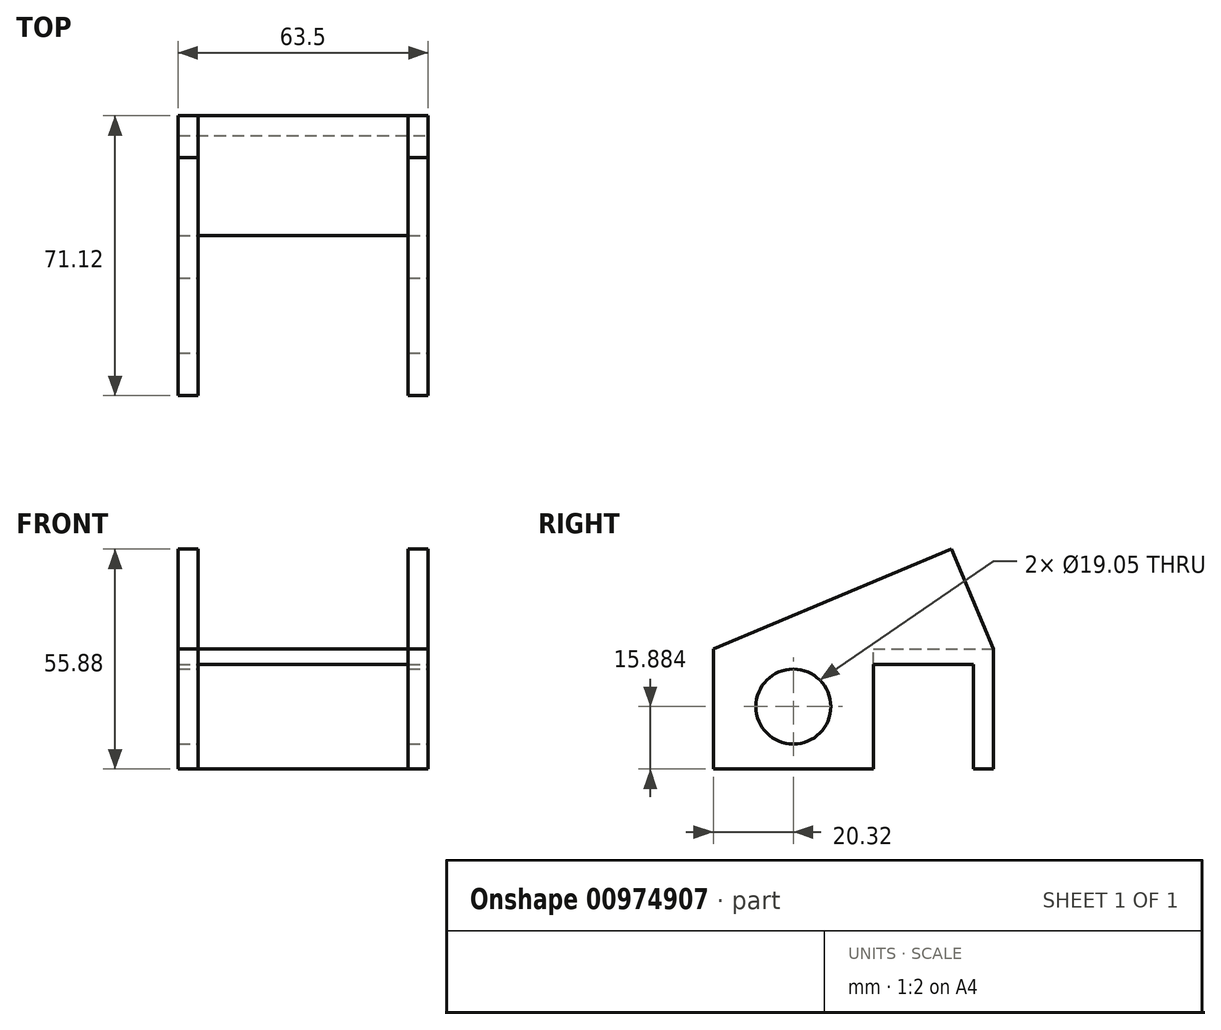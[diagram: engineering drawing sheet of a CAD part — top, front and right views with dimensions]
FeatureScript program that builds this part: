
annotation { "Feature Type Name" : "Feature", "Feature Type Description" : "" }
export const myFeature = defineFeature(function(context is Context, id is Id, definition is map)
    precondition{}
    {
        {
            var Q0;
            Q0=qCreatedBy(makeId("Front.planeOp"),FACE);
            var sketch = newSketch(context, id + "F0", { "sketchPlane" : qUnion([Q0])});
            skLineSegment(sketch, "E0.bottom", {"start": v(0, 0) * mm, "end": v(63.5, 0) * mm});
            skLineSegment(sketch, "E0.top", {"start": v(0, 30.48) * mm, "end": v(63.5, 30.48) * mm});
            skLineSegment(sketch, "E0.left", {"start": v(0, 0) * mm, "end": v(0, 30.48) * mm});
            skLineSegment(sketch, "E0.right", {"start": v(63.5, 0) * mm, "end": v(63.5, 30.48) * mm});
            skSolve(sketch);
        }
        {
            var Q0;
            Q0=makeQuery(id+"F0.imprint","IMPRINT",FACE,{"disambiguationData":[TD([[makeQuery(id+"F0.imprint","IMPRINT",EDGE,{"derivedFrom":sQuery(id+"F0.wireOp",EDGE,"E0.bottom")}),1.0]])]});
            var Q1;
            Q1 = qSketchRegion(id + "F4", true);
            extrude(context, id + "F1", {"entities" : qUnion([Q0, Q1]), "depth" : 71.12 * mm, "offsetDistance" : 25.4 * mm});
        }
        {
            var Q0;
            Q0=makeQuery(id+"F1.opExtrude","CAP_FACE",FACE,{"disambiguationData":[OSD([sQuery(id+"F0.wireOp",EDGE,"E0.bottom"),sQuery(id+"F0.wireOp",EDGE,"E0.top"),sQuery(id+"F0.wireOp",EDGE,"E0.left"),sQuery(id+"F0.wireOp",EDGE,"E0.right")])],"isStart":false});
            var sketch = newSketch(context, id + "F2", { "sketchPlane" : qUnion([Q0])});
            skLineSegment(sketch, "E1.bottom", {"start": v(5.08, 0) * mm, "end": v(58.42, 0) * mm});
            skLineSegment(sketch, "E1.top", {"start": v(5.08, 30.48) * mm, "end": v(58.42, 30.48) * mm});
            skLineSegment(sketch, "E1.left", {"start": v(5.08, 0) * mm, "end": v(5.08, 30.48) * mm});
            skLineSegment(sketch, "E1.right", {"start": v(58.42, 0) * mm, "end": v(58.42, 30.48) * mm});
            skSolve(sketch);
        }
        {
            var Q0;
            Q0=makeQuery(id+"F2.imprint","IMPRINT",FACE,{"disambiguationData":[TD([[makeQuery(id+"F2.imprint","IMPRINT",EDGE,{"derivedFrom":sQuery(id+"F2.wireOp",EDGE,"E1.bottom")}),1.0]])]});
            extrude(context, id + "F3", {"entities" : qUnion([Q0]), "operationType" : NewBodyOperationType.REMOVE, "oppositeDirection" : true, "depth" : 40.64 * mm, "offsetDistance" : 25.4 * mm});
        }
        {
            var Q0;
            Q0=makeQuery(id+"F1.opExtrude","SWEPT_FACE",FACE,{"disambiguationData":[OSD([sQuery(id+"F0.wireOp",EDGE,"E0.right")])]});
            var sketch = newSketch(context, id + "F4", { "sketchPlane" : qUnion([Q0])});
            skCircle(sketch, "E2", {"center": v(-50.8, 15.88) * mm, "radius": 9.53 * mm});
            skLineSegment(sketch, "E3.bottom", {"start": v(-5.08, 0) * mm, "end": v(-30.48, 0) * mm});
            skLineSegment(sketch, "E3.top", {"start": v(-5.08, 26.65) * mm, "end": v(-30.48, 26.65) * mm});
            skLineSegment(sketch, "E3.left", {"start": v(-5.08, 0) * mm, "end": v(-5.08, 26.65) * mm});
            skLineSegment(sketch, "E3.right", {"start": v(-30.48, 0) * mm, "end": v(-30.48, 26.65) * mm});
            skSolve(sketch);
        }
        {
            var Q0;
            Q0 = qSketchRegion(id + "F4", true);
            extrude(context, id + "F5", {"entities" : qUnion([Q0]), "operationType" : NewBodyOperationType.REMOVE, "oppositeDirection" : true, "depth" : 63.5 * mm, "offsetDistance" : 25.4 * mm});
        }
        {
            var Q0;
            Q0=makeQuery(id+"F1.opExtrude","SWEPT_FACE",FACE,{"disambiguationData":[OSD([sQuery(id+"F0.wireOp",EDGE,"E0.right")])]});
            var sketch = newSketch(context, id + "F6", { "sketchPlane" : qUnion([Q0])});
            skLineSegment(sketch, "E4", {"start": v(-71.12, 30.48) * mm, "end": v(-10.67, 55.88) * mm});
            skLineSegment(sketch, "E5", {"start": v(-10.67, 55.88) * mm, "end": v(0, 30.48) * mm});
            skSolve(sketch);
        }
        {
            var Q0;
            Q0=makeQuery(id+"F6.imprint","IMPRINT",FACE,{"disambiguationData":[TD([[makeQuery(id+"F6.imprint","IMPRINT",EDGE,{"derivedFrom":sQuery(id+"F6.wireOp",EDGE,"E4")}),-1.0]])]});
            extrude(context, id + "F7", {"entities" : qUnion([Q0]), "operationType" : NewBodyOperationType.ADD, "oppositeDirection" : true, "depth" : 5.08 * mm, "offsetDistance" : 25.4 * mm});
        }
        {
            var Q0;
            Q0=makeQuery(id+"F1.opExtrude","SWEPT_FACE",FACE,{"disambiguationData":[OSD([sQuery(id+"F0.wireOp",EDGE,"E0.left")])]});
            var sketch = newSketch(context, id + "F8", { "sketchPlane" : qUnion([Q0])});
            skLineSegment(sketch, "E6", {"start": v(0, 30.48) * mm, "end": v(10.67, 55.88) * mm});
            skLineSegment(sketch, "E7", {"start": v(10.67, 55.88) * mm, "end": v(71.12, 30.48) * mm});
            skSolve(sketch);
        }
        {
            var Q0;
            Q0=makeQuery(id+"F8.imprint","IMPRINT",FACE,{"disambiguationData":[TD([[makeQuery(id+"F8.imprint","IMPRINT",EDGE,{"derivedFrom":sQuery(id+"F8.wireOp",EDGE,"E6")}),-1.0]])]});
            extrude(context, id + "F9", {"entities" : qUnion([Q0]), "operationType" : NewBodyOperationType.ADD, "oppositeDirection" : true, "depth" : 5.08 * mm, "offsetDistance" : 25.4 * mm});
        }
    });
